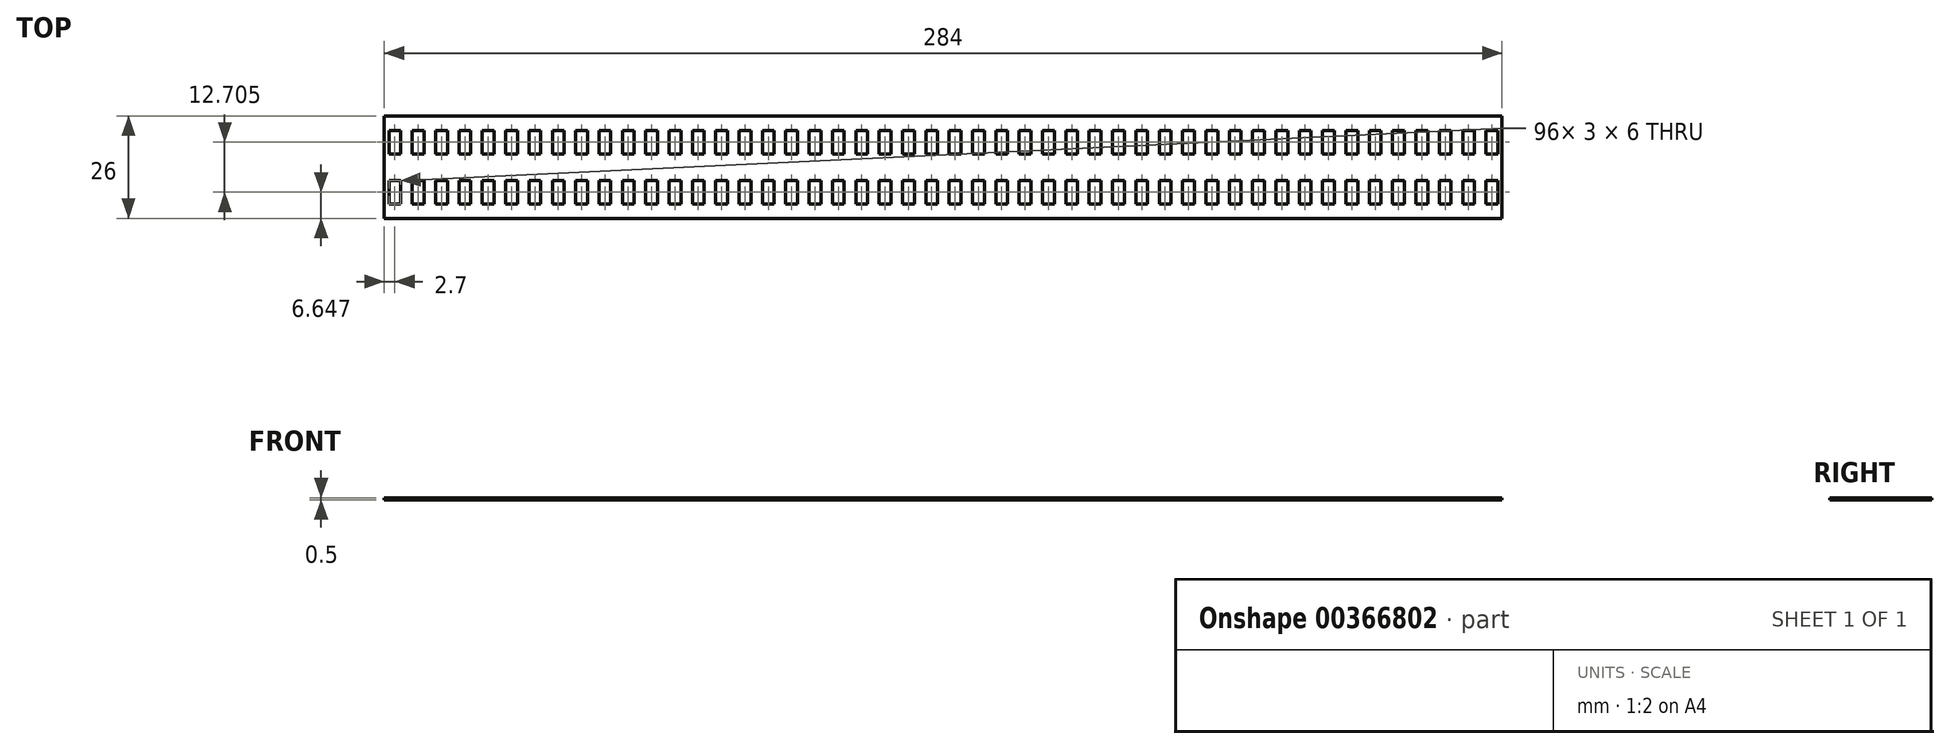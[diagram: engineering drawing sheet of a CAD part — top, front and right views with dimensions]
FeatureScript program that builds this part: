
annotation { "Feature Type Name" : "Feature", "Feature Type Description" : "" }
export const myFeature = defineFeature(function(context is Context, id is Id, definition is map)
    precondition{}
    {
        {
            var Q0;
            Q0=qCreatedBy(makeId("Top.planeOp"),FACE);
            var sketch = newSketch(context, id + "F0", { "sketchPlane" : qUnion([Q0])});
            skLineSegment(sketch, "E0.bottom", {"start": v(-142, -13) * mm, "end": v(142, -13) * mm});
            skLineSegment(sketch, "E0.top", {"start": v(-142, 13) * mm, "end": v(142, 13) * mm});
            skLineSegment(sketch, "E0.left", {"start": v(-142, -13) * mm, "end": v(-142, 13) * mm});
            skPoint(sketch, "E0.middle", {"position": v(0, 0) * mm});
            skLineSegment(sketch, "E1", {"start": v(142, 6.35) * mm, "end": v(-142, 6.35) * mm, "construction": true});
            skLineSegment(sketch, "E2.bottom", {"start": v(-140.8, 3.35) * mm, "end": v(-137.8, 3.35) * mm});
            skLineSegment(sketch, "E2.top", {"start": v(-140.8, 9.35) * mm, "end": v(-137.8, 9.35) * mm});
            skLineSegment(sketch, "E2.left", {"start": v(-140.8, 3.35) * mm, "end": v(-140.8, 9.35) * mm});
            skLineSegment(sketch, "E2.right", {"start": v(-137.8, 3.35) * mm, "end": v(-137.8, 9.35) * mm});
            skPoint(sketch, "E2.middle", {"position": v(-139.3, 6.35) * mm});
            skLineSegment(sketch, "E3.1.0.0", {"start": v(-134.87, 9.35) * mm, "end": v(-131.87, 9.35) * mm});
            skLineSegment(sketch, "E3.1.0.1", {"start": v(-134.87, 3.35) * mm, "end": v(-134.87, 9.35) * mm});
            skLineSegment(sketch, "E3.1.0.2", {"start": v(-134.87, 3.35) * mm, "end": v(-131.87, 3.35) * mm});
            skLineSegment(sketch, "E3.1.0.3", {"start": v(-131.87, 3.35) * mm, "end": v(-131.87, 9.35) * mm});
            skLineSegment(sketch, "E3.2.0.0", {"start": v(-128.94, 9.35) * mm, "end": v(-125.94, 9.35) * mm});
            skLineSegment(sketch, "E3.2.0.1", {"start": v(-128.94, 3.35) * mm, "end": v(-128.94, 9.35) * mm});
            skLineSegment(sketch, "E3.2.0.2", {"start": v(-128.94, 3.35) * mm, "end": v(-125.94, 3.35) * mm});
            skLineSegment(sketch, "E3.2.0.3", {"start": v(-125.94, 3.35) * mm, "end": v(-125.94, 9.35) * mm});
            skLineSegment(sketch, "E3.3.0.0", {"start": v(-123.01, 9.35) * mm, "end": v(-120.01, 9.35) * mm});
            skLineSegment(sketch, "E3.3.0.1", {"start": v(-123.01, 3.35) * mm, "end": v(-123.01, 9.35) * mm});
            skLineSegment(sketch, "E3.3.0.2", {"start": v(-123.01, 3.35) * mm, "end": v(-120.01, 3.35) * mm});
            skLineSegment(sketch, "E3.3.0.3", {"start": v(-120.01, 3.35) * mm, "end": v(-120.01, 9.35) * mm});
            skLineSegment(sketch, "E3.4.0.0", {"start": v(-117.08, 9.35) * mm, "end": v(-114.08, 9.35) * mm});
            skLineSegment(sketch, "E3.4.0.1", {"start": v(-117.08, 3.35) * mm, "end": v(-117.08, 9.35) * mm});
            skLineSegment(sketch, "E3.4.0.2", {"start": v(-117.08, 3.35) * mm, "end": v(-114.08, 3.35) * mm});
            skLineSegment(sketch, "E3.4.0.3", {"start": v(-114.08, 3.35) * mm, "end": v(-114.08, 9.35) * mm});
            skLineSegment(sketch, "E3.5.0.0", {"start": v(-111.15, 9.35) * mm, "end": v(-108.15, 9.35) * mm});
            skLineSegment(sketch, "E3.5.0.1", {"start": v(-111.15, 3.35) * mm, "end": v(-111.15, 9.35) * mm});
            skLineSegment(sketch, "E3.5.0.2", {"start": v(-111.15, 3.35) * mm, "end": v(-108.15, 3.35) * mm});
            skLineSegment(sketch, "E3.5.0.3", {"start": v(-108.15, 3.35) * mm, "end": v(-108.15, 9.35) * mm});
            skLineSegment(sketch, "E3.6.0.0", {"start": v(-105.22, 9.35) * mm, "end": v(-102.22, 9.35) * mm});
            skLineSegment(sketch, "E3.6.0.1", {"start": v(-105.22, 3.35) * mm, "end": v(-105.22, 9.35) * mm});
            skLineSegment(sketch, "E3.6.0.2", {"start": v(-105.22, 3.35) * mm, "end": v(-102.22, 3.35) * mm});
            skLineSegment(sketch, "E3.6.0.3", {"start": v(-102.22, 3.35) * mm, "end": v(-102.22, 9.35) * mm});
            skLineSegment(sketch, "E3.7.0.0", {"start": v(-99.3, 9.35) * mm, "end": v(-96.3, 9.35) * mm});
            skLineSegment(sketch, "E3.7.0.1", {"start": v(-99.3, 3.35) * mm, "end": v(-99.3, 9.35) * mm});
            skLineSegment(sketch, "E3.7.0.2", {"start": v(-99.3, 3.35) * mm, "end": v(-96.3, 3.35) * mm});
            skLineSegment(sketch, "E3.7.0.3", {"start": v(-96.3, 3.35) * mm, "end": v(-96.3, 9.35) * mm});
            skLineSegment(sketch, "E3.8.0.0", {"start": v(-93.36, 9.35) * mm, "end": v(-90.36, 9.35) * mm});
            skLineSegment(sketch, "E3.8.0.1", {"start": v(-93.36, 3.35) * mm, "end": v(-93.36, 9.35) * mm});
            skLineSegment(sketch, "E3.8.0.2", {"start": v(-93.36, 3.35) * mm, "end": v(-90.36, 3.35) * mm});
            skLineSegment(sketch, "E3.8.0.3", {"start": v(-90.36, 3.35) * mm, "end": v(-90.36, 9.35) * mm});
            skLineSegment(sketch, "E3.9.0.0", {"start": v(-87.43, 9.35) * mm, "end": v(-84.43, 9.35) * mm});
            skLineSegment(sketch, "E3.9.0.1", {"start": v(-87.43, 3.35) * mm, "end": v(-87.43, 9.35) * mm});
            skLineSegment(sketch, "E3.9.0.2", {"start": v(-87.43, 3.35) * mm, "end": v(-84.43, 3.35) * mm});
            skLineSegment(sketch, "E3.9.0.3", {"start": v(-84.43, 3.35) * mm, "end": v(-84.43, 9.35) * mm});
            skLineSegment(sketch, "E3.10.0.0", {"start": v(-81.5, 9.35) * mm, "end": v(-78.5, 9.35) * mm});
            skLineSegment(sketch, "E3.10.0.1", {"start": v(-81.5, 3.35) * mm, "end": v(-81.5, 9.35) * mm});
            skLineSegment(sketch, "E3.10.0.2", {"start": v(-81.5, 3.35) * mm, "end": v(-78.5, 3.35) * mm});
            skLineSegment(sketch, "E3.10.0.3", {"start": v(-78.5, 3.35) * mm, "end": v(-78.5, 9.35) * mm});
            skLineSegment(sketch, "E3.11.0.0", {"start": v(-75.57, 9.35) * mm, "end": v(-72.57, 9.35) * mm});
            skLineSegment(sketch, "E3.11.0.1", {"start": v(-75.57, 3.35) * mm, "end": v(-75.57, 9.35) * mm});
            skLineSegment(sketch, "E3.11.0.2", {"start": v(-75.57, 3.35) * mm, "end": v(-72.57, 3.35) * mm});
            skLineSegment(sketch, "E3.11.0.3", {"start": v(-72.57, 3.35) * mm, "end": v(-72.57, 9.35) * mm});
            skLineSegment(sketch, "E3.12.0.0", {"start": v(-69.64, 9.35) * mm, "end": v(-66.64, 9.35) * mm});
            skLineSegment(sketch, "E3.12.0.1", {"start": v(-69.64, 3.35) * mm, "end": v(-69.64, 9.35) * mm});
            skLineSegment(sketch, "E3.12.0.2", {"start": v(-69.64, 3.35) * mm, "end": v(-66.64, 3.35) * mm});
            skLineSegment(sketch, "E3.12.0.3", {"start": v(-66.64, 3.35) * mm, "end": v(-66.64, 9.35) * mm});
            skLineSegment(sketch, "E3.13.0.0", {"start": v(-63.71, 9.35) * mm, "end": v(-60.71, 9.35) * mm});
            skLineSegment(sketch, "E3.13.0.1", {"start": v(-63.71, 3.35) * mm, "end": v(-63.71, 9.35) * mm});
            skLineSegment(sketch, "E3.13.0.2", {"start": v(-63.71, 3.35) * mm, "end": v(-60.71, 3.35) * mm});
            skLineSegment(sketch, "E3.13.0.3", {"start": v(-60.71, 3.35) * mm, "end": v(-60.71, 9.35) * mm});
            skLineSegment(sketch, "E3.14.0.0", {"start": v(-57.78, 9.35) * mm, "end": v(-54.78, 9.35) * mm});
            skLineSegment(sketch, "E3.14.0.1", {"start": v(-57.78, 3.35) * mm, "end": v(-57.78, 9.35) * mm});
            skLineSegment(sketch, "E3.14.0.2", {"start": v(-57.78, 3.35) * mm, "end": v(-54.78, 3.35) * mm});
            skLineSegment(sketch, "E3.14.0.3", {"start": v(-54.78, 3.35) * mm, "end": v(-54.78, 9.35) * mm});
            skLineSegment(sketch, "E3.15.0.0", {"start": v(-51.85, 9.35) * mm, "end": v(-48.85, 9.35) * mm});
            skLineSegment(sketch, "E3.15.0.1", {"start": v(-51.85, 3.35) * mm, "end": v(-51.85, 9.35) * mm});
            skLineSegment(sketch, "E3.15.0.2", {"start": v(-51.85, 3.35) * mm, "end": v(-48.85, 3.35) * mm});
            skLineSegment(sketch, "E3.15.0.3", {"start": v(-48.85, 3.35) * mm, "end": v(-48.85, 9.35) * mm});
            skLineSegment(sketch, "E3.16.0.0", {"start": v(-45.92, 9.35) * mm, "end": v(-42.92, 9.35) * mm});
            skLineSegment(sketch, "E3.16.0.1", {"start": v(-45.92, 3.35) * mm, "end": v(-45.92, 9.35) * mm});
            skLineSegment(sketch, "E3.16.0.2", {"start": v(-45.92, 3.35) * mm, "end": v(-42.92, 3.35) * mm});
            skLineSegment(sketch, "E3.16.0.3", {"start": v(-42.92, 3.35) * mm, "end": v(-42.92, 9.35) * mm});
            skLineSegment(sketch, "E3.17.0.0", {"start": v(-40, 9.35) * mm, "end": v(-37, 9.35) * mm});
            skLineSegment(sketch, "E3.17.0.1", {"start": v(-40, 3.35) * mm, "end": v(-40, 9.35) * mm});
            skLineSegment(sketch, "E3.17.0.2", {"start": v(-40, 3.35) * mm, "end": v(-37, 3.35) * mm});
            skLineSegment(sketch, "E3.17.0.3", {"start": v(-37, 3.35) * mm, "end": v(-37, 9.35) * mm});
            skLineSegment(sketch, "E3.18.0.0", {"start": v(-34.06, 9.35) * mm, "end": v(-31.06, 9.35) * mm});
            skLineSegment(sketch, "E3.18.0.1", {"start": v(-34.06, 3.35) * mm, "end": v(-34.06, 9.35) * mm});
            skLineSegment(sketch, "E3.18.0.2", {"start": v(-34.06, 3.35) * mm, "end": v(-31.06, 3.35) * mm});
            skLineSegment(sketch, "E3.18.0.3", {"start": v(-31.06, 3.35) * mm, "end": v(-31.06, 9.35) * mm});
            skLineSegment(sketch, "E3.19.0.0", {"start": v(-28.13, 9.35) * mm, "end": v(-25.13, 9.35) * mm});
            skLineSegment(sketch, "E3.19.0.1", {"start": v(-28.13, 3.35) * mm, "end": v(-28.13, 9.35) * mm});
            skLineSegment(sketch, "E3.19.0.2", {"start": v(-28.13, 3.35) * mm, "end": v(-25.13, 3.35) * mm});
            skLineSegment(sketch, "E3.19.0.3", {"start": v(-25.13, 3.35) * mm, "end": v(-25.13, 9.35) * mm});
            skLineSegment(sketch, "E3.20.0.0", {"start": v(-22.2, 9.35) * mm, "end": v(-19.2, 9.35) * mm});
            skLineSegment(sketch, "E3.20.0.1", {"start": v(-22.2, 3.35) * mm, "end": v(-22.2, 9.35) * mm});
            skLineSegment(sketch, "E3.20.0.2", {"start": v(-22.2, 3.35) * mm, "end": v(-19.2, 3.35) * mm});
            skLineSegment(sketch, "E3.20.0.3", {"start": v(-19.2, 3.35) * mm, "end": v(-19.2, 9.35) * mm});
            skLineSegment(sketch, "E3.21.0.0", {"start": v(-16.27, 9.35) * mm, "end": v(-13.27, 9.35) * mm});
            skLineSegment(sketch, "E3.21.0.1", {"start": v(-16.27, 3.35) * mm, "end": v(-16.27, 9.35) * mm});
            skLineSegment(sketch, "E3.21.0.2", {"start": v(-16.27, 3.35) * mm, "end": v(-13.27, 3.35) * mm});
            skLineSegment(sketch, "E3.21.0.3", {"start": v(-13.27, 3.35) * mm, "end": v(-13.27, 9.35) * mm});
            skLineSegment(sketch, "E3.22.0.0", {"start": v(-10.34, 9.35) * mm, "end": v(-7.34, 9.35) * mm});
            skLineSegment(sketch, "E3.22.0.1", {"start": v(-10.34, 3.35) * mm, "end": v(-10.34, 9.35) * mm});
            skLineSegment(sketch, "E3.22.0.2", {"start": v(-10.34, 3.35) * mm, "end": v(-7.34, 3.35) * mm});
            skLineSegment(sketch, "E3.22.0.3", {"start": v(-7.34, 3.35) * mm, "end": v(-7.34, 9.35) * mm});
            skLineSegment(sketch, "E3.23.0.0", {"start": v(-4.41, 9.35) * mm, "end": v(-1.41, 9.35) * mm});
            skLineSegment(sketch, "E3.23.0.1", {"start": v(-4.41, 3.35) * mm, "end": v(-4.41, 9.35) * mm});
            skLineSegment(sketch, "E3.23.0.2", {"start": v(-4.41, 3.35) * mm, "end": v(-1.41, 3.35) * mm});
            skLineSegment(sketch, "E3.23.0.3", {"start": v(-1.41, 3.35) * mm, "end": v(-1.41, 9.35) * mm});
            skLineSegment(sketch, "E3.24.0.0", {"start": v(1.52, 9.35) * mm, "end": v(4.52, 9.35) * mm});
            skLineSegment(sketch, "E3.24.0.1", {"start": v(1.52, 3.35) * mm, "end": v(1.52, 9.35) * mm});
            skLineSegment(sketch, "E3.24.0.2", {"start": v(1.52, 3.35) * mm, "end": v(4.52, 3.35) * mm});
            skLineSegment(sketch, "E3.24.0.3", {"start": v(4.52, 3.35) * mm, "end": v(4.52, 9.35) * mm});
            skLineSegment(sketch, "E3.25.0.0", {"start": v(7.45, 9.35) * mm, "end": v(10.45, 9.35) * mm});
            skLineSegment(sketch, "E3.25.0.1", {"start": v(7.45, 3.35) * mm, "end": v(7.45, 9.35) * mm});
            skLineSegment(sketch, "E3.25.0.2", {"start": v(7.45, 3.35) * mm, "end": v(10.45, 3.35) * mm});
            skLineSegment(sketch, "E3.25.0.3", {"start": v(10.45, 3.35) * mm, "end": v(10.45, 9.35) * mm});
            skLineSegment(sketch, "E3.26.0.0", {"start": v(13.38, 9.35) * mm, "end": v(16.38, 9.35) * mm});
            skLineSegment(sketch, "E3.26.0.1", {"start": v(13.38, 3.35) * mm, "end": v(13.38, 9.35) * mm});
            skLineSegment(sketch, "E3.26.0.2", {"start": v(13.38, 3.35) * mm, "end": v(16.38, 3.35) * mm});
            skLineSegment(sketch, "E3.26.0.3", {"start": v(16.38, 3.35) * mm, "end": v(16.38, 9.35) * mm});
            skLineSegment(sketch, "E3.27.0.0", {"start": v(19.3, 9.35) * mm, "end": v(22.3, 9.35) * mm});
            skLineSegment(sketch, "E3.27.0.1", {"start": v(19.3, 3.35) * mm, "end": v(19.3, 9.35) * mm});
            skLineSegment(sketch, "E3.27.0.2", {"start": v(19.3, 3.35) * mm, "end": v(22.3, 3.35) * mm});
            skLineSegment(sketch, "E3.27.0.3", {"start": v(22.3, 3.35) * mm, "end": v(22.3, 9.35) * mm});
            skLineSegment(sketch, "E3.28.0.0", {"start": v(25.24, 9.35) * mm, "end": v(28.24, 9.35) * mm});
            skLineSegment(sketch, "E3.28.0.1", {"start": v(25.24, 3.35) * mm, "end": v(25.24, 9.35) * mm});
            skLineSegment(sketch, "E3.28.0.2", {"start": v(25.24, 3.35) * mm, "end": v(28.24, 3.35) * mm});
            skLineSegment(sketch, "E3.28.0.3", {"start": v(28.24, 3.35) * mm, "end": v(28.24, 9.35) * mm});
            skLineSegment(sketch, "E3.29.0.0", {"start": v(31.17, 9.35) * mm, "end": v(34.17, 9.35) * mm});
            skLineSegment(sketch, "E3.29.0.1", {"start": v(31.17, 3.35) * mm, "end": v(31.17, 9.35) * mm});
            skLineSegment(sketch, "E3.29.0.2", {"start": v(31.17, 3.35) * mm, "end": v(34.17, 3.35) * mm});
            skLineSegment(sketch, "E3.29.0.3", {"start": v(34.17, 3.35) * mm, "end": v(34.17, 9.35) * mm});
            skLineSegment(sketch, "E3.30.0.0", {"start": v(37.1, 9.35) * mm, "end": v(40.1, 9.35) * mm});
            skLineSegment(sketch, "E3.30.0.1", {"start": v(37.1, 3.35) * mm, "end": v(37.1, 9.35) * mm});
            skLineSegment(sketch, "E3.30.0.2", {"start": v(37.1, 3.35) * mm, "end": v(40.1, 3.35) * mm});
            skLineSegment(sketch, "E3.30.0.3", {"start": v(40.1, 3.35) * mm, "end": v(40.1, 9.35) * mm});
            skLineSegment(sketch, "E3.31.0.0", {"start": v(43.03, 9.35) * mm, "end": v(46.03, 9.35) * mm});
            skLineSegment(sketch, "E3.31.0.1", {"start": v(43.03, 3.35) * mm, "end": v(43.03, 9.35) * mm});
            skLineSegment(sketch, "E3.31.0.2", {"start": v(43.03, 3.35) * mm, "end": v(46.03, 3.35) * mm});
            skLineSegment(sketch, "E3.31.0.3", {"start": v(46.03, 3.35) * mm, "end": v(46.03, 9.35) * mm});
            skLineSegment(sketch, "E3.32.0.0", {"start": v(48.96, 9.35) * mm, "end": v(51.96, 9.35) * mm});
            skLineSegment(sketch, "E3.32.0.1", {"start": v(48.96, 3.35) * mm, "end": v(48.96, 9.35) * mm});
            skLineSegment(sketch, "E3.32.0.2", {"start": v(48.96, 3.35) * mm, "end": v(51.96, 3.35) * mm});
            skLineSegment(sketch, "E3.32.0.3", {"start": v(51.96, 3.35) * mm, "end": v(51.96, 9.35) * mm});
            skLineSegment(sketch, "E3.33.0.0", {"start": v(54.89, 9.35) * mm, "end": v(57.89, 9.35) * mm});
            skLineSegment(sketch, "E3.33.0.1", {"start": v(54.89, 3.35) * mm, "end": v(54.89, 9.35) * mm});
            skLineSegment(sketch, "E3.33.0.2", {"start": v(54.89, 3.35) * mm, "end": v(57.89, 3.35) * mm});
            skLineSegment(sketch, "E3.33.0.3", {"start": v(57.89, 3.35) * mm, "end": v(57.89, 9.35) * mm});
            skLineSegment(sketch, "E3.34.0.0", {"start": v(60.82, 9.35) * mm, "end": v(63.82, 9.35) * mm});
            skLineSegment(sketch, "E3.34.0.1", {"start": v(60.82, 3.35) * mm, "end": v(60.82, 9.35) * mm});
            skLineSegment(sketch, "E3.34.0.2", {"start": v(60.82, 3.35) * mm, "end": v(63.82, 3.35) * mm});
            skLineSegment(sketch, "E3.34.0.3", {"start": v(63.82, 3.35) * mm, "end": v(63.82, 9.35) * mm});
            skLineSegment(sketch, "E3.35.0.0", {"start": v(66.75, 9.35) * mm, "end": v(69.75, 9.35) * mm});
            skLineSegment(sketch, "E3.35.0.1", {"start": v(66.75, 3.35) * mm, "end": v(66.75, 9.35) * mm});
            skLineSegment(sketch, "E3.35.0.2", {"start": v(66.75, 3.35) * mm, "end": v(69.75, 3.35) * mm});
            skLineSegment(sketch, "E3.35.0.3", {"start": v(69.75, 3.35) * mm, "end": v(69.75, 9.35) * mm});
            skLineSegment(sketch, "E3.36.0.0", {"start": v(72.68, 9.35) * mm, "end": v(75.68, 9.35) * mm});
            skLineSegment(sketch, "E3.36.0.1", {"start": v(72.68, 3.35) * mm, "end": v(72.68, 9.35) * mm});
            skLineSegment(sketch, "E3.36.0.2", {"start": v(72.68, 3.35) * mm, "end": v(75.68, 3.35) * mm});
            skLineSegment(sketch, "E3.36.0.3", {"start": v(75.68, 3.35) * mm, "end": v(75.68, 9.35) * mm});
            skLineSegment(sketch, "E3.37.0.0", {"start": v(78.6, 9.35) * mm, "end": v(81.6, 9.35) * mm});
            skLineSegment(sketch, "E3.37.0.1", {"start": v(78.6, 3.35) * mm, "end": v(78.6, 9.35) * mm});
            skLineSegment(sketch, "E3.37.0.2", {"start": v(78.6, 3.35) * mm, "end": v(81.6, 3.35) * mm});
            skLineSegment(sketch, "E3.37.0.3", {"start": v(81.6, 3.35) * mm, "end": v(81.6, 9.35) * mm});
            skLineSegment(sketch, "E3.38.0.0", {"start": v(84.54, 9.35) * mm, "end": v(87.54, 9.35) * mm});
            skLineSegment(sketch, "E3.38.0.1", {"start": v(84.54, 3.35) * mm, "end": v(84.54, 9.35) * mm});
            skLineSegment(sketch, "E3.38.0.2", {"start": v(84.54, 3.35) * mm, "end": v(87.54, 3.35) * mm});
            skLineSegment(sketch, "E3.38.0.3", {"start": v(87.54, 3.35) * mm, "end": v(87.54, 9.35) * mm});
            skLineSegment(sketch, "E3.39.0.0", {"start": v(90.47, 9.35) * mm, "end": v(93.47, 9.35) * mm});
            skLineSegment(sketch, "E3.39.0.1", {"start": v(90.47, 3.35) * mm, "end": v(90.47, 9.35) * mm});
            skLineSegment(sketch, "E3.39.0.2", {"start": v(90.47, 3.35) * mm, "end": v(93.47, 3.35) * mm});
            skLineSegment(sketch, "E3.39.0.3", {"start": v(93.47, 3.35) * mm, "end": v(93.47, 9.35) * mm});
            skLineSegment(sketch, "E3.40.0.0", {"start": v(96.4, 9.35) * mm, "end": v(99.4, 9.35) * mm});
            skLineSegment(sketch, "E3.40.0.1", {"start": v(96.4, 3.35) * mm, "end": v(96.4, 9.35) * mm});
            skLineSegment(sketch, "E3.40.0.2", {"start": v(96.4, 3.35) * mm, "end": v(99.4, 3.35) * mm});
            skLineSegment(sketch, "E3.40.0.3", {"start": v(99.4, 3.35) * mm, "end": v(99.4, 9.35) * mm});
            skLineSegment(sketch, "E3.41.0.0", {"start": v(102.33, 9.35) * mm, "end": v(105.33, 9.35) * mm});
            skLineSegment(sketch, "E3.41.0.1", {"start": v(102.33, 3.35) * mm, "end": v(102.33, 9.35) * mm});
            skLineSegment(sketch, "E3.41.0.2", {"start": v(102.33, 3.35) * mm, "end": v(105.33, 3.35) * mm});
            skLineSegment(sketch, "E3.41.0.3", {"start": v(105.33, 3.35) * mm, "end": v(105.33, 9.35) * mm});
            skLineSegment(sketch, "E3.42.0.0", {"start": v(108.26, 9.35) * mm, "end": v(111.26, 9.35) * mm});
            skLineSegment(sketch, "E3.42.0.1", {"start": v(108.26, 3.35) * mm, "end": v(108.26, 9.35) * mm});
            skLineSegment(sketch, "E3.42.0.2", {"start": v(108.26, 3.35) * mm, "end": v(111.26, 3.35) * mm});
            skLineSegment(sketch, "E3.42.0.3", {"start": v(111.26, 3.35) * mm, "end": v(111.26, 9.35) * mm});
            skLineSegment(sketch, "E3.43.0.0", {"start": v(114.19, 9.35) * mm, "end": v(117.19, 9.35) * mm});
            skLineSegment(sketch, "E3.43.0.1", {"start": v(114.19, 3.35) * mm, "end": v(114.19, 9.35) * mm});
            skLineSegment(sketch, "E3.43.0.2", {"start": v(114.19, 3.35) * mm, "end": v(117.19, 3.35) * mm});
            skLineSegment(sketch, "E3.43.0.3", {"start": v(117.19, 3.35) * mm, "end": v(117.19, 9.35) * mm});
            skLineSegment(sketch, "E3.44.0.0", {"start": v(120.12, 9.35) * mm, "end": v(123.12, 9.35) * mm});
            skLineSegment(sketch, "E3.44.0.1", {"start": v(120.12, 3.35) * mm, "end": v(120.12, 9.35) * mm});
            skLineSegment(sketch, "E3.44.0.2", {"start": v(120.12, 3.35) * mm, "end": v(123.12, 3.35) * mm});
            skLineSegment(sketch, "E3.44.0.3", {"start": v(123.12, 3.35) * mm, "end": v(123.12, 9.35) * mm});
            skLineSegment(sketch, "E3.45.0.0", {"start": v(126.05, 9.35) * mm, "end": v(129.05, 9.35) * mm});
            skLineSegment(sketch, "E3.45.0.1", {"start": v(126.05, 3.35) * mm, "end": v(126.05, 9.35) * mm});
            skLineSegment(sketch, "E3.45.0.2", {"start": v(126.05, 3.35) * mm, "end": v(129.05, 3.35) * mm});
            skLineSegment(sketch, "E3.45.0.3", {"start": v(129.05, 3.35) * mm, "end": v(129.05, 9.35) * mm});
            skLineSegment(sketch, "E3.46.0.0", {"start": v(131.98, 9.35) * mm, "end": v(134.98, 9.35) * mm});
            skLineSegment(sketch, "E3.46.0.1", {"start": v(131.98, 3.35) * mm, "end": v(131.98, 9.35) * mm});
            skLineSegment(sketch, "E3.46.0.2", {"start": v(131.98, 3.35) * mm, "end": v(134.98, 3.35) * mm});
            skLineSegment(sketch, "E3.46.0.3", {"start": v(134.98, 3.35) * mm, "end": v(134.98, 9.35) * mm});
            skLineSegment(sketch, "E3.47.0.0", {"start": v(137.9, 9.35) * mm, "end": v(140.9, 9.35) * mm});
            skLineSegment(sketch, "E3.47.0.1", {"start": v(137.9, 3.35) * mm, "end": v(137.9, 9.35) * mm});
            skLineSegment(sketch, "E3.47.0.2", {"start": v(137.9, 3.35) * mm, "end": v(140.9, 3.35) * mm});
            skLineSegment(sketch, "E3.47.0.3", {"start": v(140.9, 3.35) * mm, "end": v(140.9, 9.35) * mm});
            skLineSegment(sketch, "E3.direction1", {"start": v(-140.8, 9.35) * mm, "end": v(-134.87, 9.35) * mm, "construction": true});
            skLineSegment(sketch, "E4", {"start": v(-142, 0) * mm, "end": v(142, 0) * mm});
            skLineSegment(sketch, "E5", {"start": v(142, 13) * mm, "end": v(142, 0) * mm});
            skLineSegment(sketch, "E6", {"start": v(142, 0) * mm, "end": v(142, -13) * mm});
            skLineSegment(sketch, "E7.MirrorCS", {"start": v(90.47, -3.35) * mm, "end": v(90.47, -9.35) * mm});
            skLineSegment(sketch, "E8.MirrorCS", {"start": v(114.19, -3.35) * mm, "end": v(114.19, -9.35) * mm});
            skLineSegment(sketch, "E9.MirrorCS", {"start": v(137.9, -3.35) * mm, "end": v(137.9, -9.35) * mm});
            skLineSegment(sketch, "E10.MirrorCS", {"start": v(43.03, -3.35) * mm, "end": v(43.03, -9.35) * mm});
            skLineSegment(sketch, "E11.MirrorCS", {"start": v(66.75, -3.35) * mm, "end": v(66.75, -9.35) * mm});
            skLineSegment(sketch, "E12.MirrorCS", {"start": v(43.03, -9.35) * mm, "end": v(46.03, -9.35) * mm});
            skLineSegment(sketch, "E13.MirrorCS", {"start": v(66.75, -9.35) * mm, "end": v(69.75, -9.35) * mm});
            skLineSegment(sketch, "E14.MirrorCS", {"start": v(90.47, -9.35) * mm, "end": v(93.47, -9.35) * mm});
            skLineSegment(sketch, "E15.MirrorCS", {"start": v(114.19, -9.35) * mm, "end": v(117.19, -9.35) * mm});
            skLineSegment(sketch, "E16.MirrorCS", {"start": v(87.54, -3.35) * mm, "end": v(87.54, -9.35) * mm});
            skLineSegment(sketch, "E17.MirrorCS", {"start": v(111.26, -3.35) * mm, "end": v(111.26, -9.35) * mm});
            skLineSegment(sketch, "E18.MirrorCS", {"start": v(134.98, -3.35) * mm, "end": v(134.98, -9.35) * mm});
            skLineSegment(sketch, "E19.MirrorCS", {"start": v(40.1, -3.35) * mm, "end": v(40.1, -9.35) * mm});
            skLineSegment(sketch, "E20.MirrorCS", {"start": v(63.82, -3.35) * mm, "end": v(63.82, -9.35) * mm});
            skLineSegment(sketch, "E21.MirrorCS", {"start": v(84.54, -3.35) * mm, "end": v(87.54, -3.35) * mm});
            skLineSegment(sketch, "E22.MirrorCS", {"start": v(108.26, -3.35) * mm, "end": v(111.26, -3.35) * mm});
            skLineSegment(sketch, "E23.MirrorCS", {"start": v(131.98, -3.35) * mm, "end": v(134.98, -3.35) * mm});
            skLineSegment(sketch, "E24.MirrorCS", {"start": v(60.82, -3.35) * mm, "end": v(63.82, -3.35) * mm});
            skLineSegment(sketch, "E25.MirrorCS", {"start": v(84.54, -3.35) * mm, "end": v(84.54, -9.35) * mm});
            skLineSegment(sketch, "E26.MirrorCS", {"start": v(108.26, -3.35) * mm, "end": v(108.26, -9.35) * mm});
            skLineSegment(sketch, "E27.MirrorCS", {"start": v(131.98, -3.35) * mm, "end": v(131.98, -9.35) * mm});
            skLineSegment(sketch, "E28.MirrorCS", {"start": v(60.82, -3.35) * mm, "end": v(60.82, -9.35) * mm});
            skLineSegment(sketch, "E29.MirrorCS", {"start": v(57.89, -3.35) * mm, "end": v(57.89, -9.35) * mm});
            skLineSegment(sketch, "E30.MirrorCS", {"start": v(81.6, -3.35) * mm, "end": v(81.6, -9.35) * mm});
            skLineSegment(sketch, "E31.MirrorCS", {"start": v(105.33, -3.35) * mm, "end": v(105.33, -9.35) * mm});
            skLineSegment(sketch, "E32.MirrorCS", {"start": v(129.05, -3.35) * mm, "end": v(129.05, -9.35) * mm});
            skLineSegment(sketch, "E33.MirrorCS", {"start": v(84.54, -9.35) * mm, "end": v(87.54, -9.35) * mm});
            skLineSegment(sketch, "E34.MirrorCS", {"start": v(108.26, -9.35) * mm, "end": v(111.26, -9.35) * mm});
            skLineSegment(sketch, "E35.MirrorCS", {"start": v(131.98, -9.35) * mm, "end": v(134.98, -9.35) * mm});
            skLineSegment(sketch, "E36.MirrorCS", {"start": v(60.82, -9.35) * mm, "end": v(63.82, -9.35) * mm});
            skLineSegment(sketch, "E37.MirrorCS", {"start": v(54.89, -3.35) * mm, "end": v(57.89, -3.35) * mm});
            skLineSegment(sketch, "E38.MirrorCS", {"start": v(78.6, -3.35) * mm, "end": v(81.6, -3.35) * mm});
            skLineSegment(sketch, "E39.MirrorCS", {"start": v(102.33, -3.35) * mm, "end": v(105.33, -3.35) * mm});
            skLineSegment(sketch, "E40.MirrorCS", {"start": v(126.05, -3.35) * mm, "end": v(129.05, -3.35) * mm});
            skLineSegment(sketch, "E41.MirrorCS", {"start": v(54.89, -3.35) * mm, "end": v(54.89, -9.35) * mm});
            skLineSegment(sketch, "E42.MirrorCS", {"start": v(78.6, -3.35) * mm, "end": v(78.6, -9.35) * mm});
            skLineSegment(sketch, "E43.MirrorCS", {"start": v(126.05, -3.35) * mm, "end": v(126.05, -9.35) * mm});
            skLineSegment(sketch, "E44.MirrorCS", {"start": v(102.33, -3.35) * mm, "end": v(102.33, -9.35) * mm});
            skLineSegment(sketch, "E45.MirrorCS", {"start": v(54.89, -9.35) * mm, "end": v(57.89, -9.35) * mm});
            skLineSegment(sketch, "E46.MirrorCS", {"start": v(78.6, -9.35) * mm, "end": v(81.6, -9.35) * mm});
            skLineSegment(sketch, "E47.MirrorCS", {"start": v(102.33, -9.35) * mm, "end": v(105.33, -9.35) * mm});
            skLineSegment(sketch, "E48.MirrorCS", {"start": v(126.05, -9.35) * mm, "end": v(129.05, -9.35) * mm});
            skLineSegment(sketch, "E49.MirrorCS", {"start": v(51.96, -3.35) * mm, "end": v(51.96, -9.35) * mm});
            skLineSegment(sketch, "E50.MirrorCS", {"start": v(75.68, -3.35) * mm, "end": v(75.68, -9.35) * mm});
            skLineSegment(sketch, "E51.MirrorCS", {"start": v(99.4, -3.35) * mm, "end": v(99.4, -9.35) * mm});
            skLineSegment(sketch, "E52.MirrorCS", {"start": v(123.12, -3.35) * mm, "end": v(123.12, -9.35) * mm});
            skLineSegment(sketch, "E53.MirrorCS", {"start": v(48.96, -3.35) * mm, "end": v(51.96, -3.35) * mm});
            skLineSegment(sketch, "E54.MirrorCS", {"start": v(72.68, -3.35) * mm, "end": v(75.68, -3.35) * mm});
            skLineSegment(sketch, "E55.MirrorCS", {"start": v(96.4, -3.35) * mm, "end": v(99.4, -3.35) * mm});
            skLineSegment(sketch, "E56.MirrorCS", {"start": v(120.12, -3.35) * mm, "end": v(123.12, -3.35) * mm});
            skLineSegment(sketch, "E57.MirrorCS", {"start": v(96.4, -3.35) * mm, "end": v(96.4, -9.35) * mm});
            skLineSegment(sketch, "E58.MirrorCS", {"start": v(120.12, -3.35) * mm, "end": v(120.12, -9.35) * mm});
            skLineSegment(sketch, "E59.MirrorCS", {"start": v(48.96, -3.35) * mm, "end": v(48.96, -9.35) * mm});
            skLineSegment(sketch, "E60.MirrorCS", {"start": v(72.68, -3.35) * mm, "end": v(72.68, -9.35) * mm});
            skLineSegment(sketch, "E61.MirrorCS", {"start": v(96.4, -9.35) * mm, "end": v(99.4, -9.35) * mm});
            skLineSegment(sketch, "E62.MirrorCS", {"start": v(120.12, -9.35) * mm, "end": v(123.12, -9.35) * mm});
            skLineSegment(sketch, "E63.MirrorCS", {"start": v(48.96, -9.35) * mm, "end": v(51.96, -9.35) * mm});
            skLineSegment(sketch, "E64.MirrorCS", {"start": v(72.68, -9.35) * mm, "end": v(75.68, -9.35) * mm});
            skLineSegment(sketch, "E65.MirrorCS", {"start": v(93.47, -3.35) * mm, "end": v(93.47, -9.35) * mm});
            skLineSegment(sketch, "E66.MirrorCS", {"start": v(117.19, -3.35) * mm, "end": v(117.19, -9.35) * mm});
            skLineSegment(sketch, "E67.MirrorCS", {"start": v(46.03, -3.35) * mm, "end": v(46.03, -9.35) * mm});
            skLineSegment(sketch, "E68.MirrorCS", {"start": v(69.75, -3.35) * mm, "end": v(69.75, -9.35) * mm});
            skLineSegment(sketch, "E69.MirrorCS", {"start": v(90.47, -3.35) * mm, "end": v(93.47, -3.35) * mm});
            skLineSegment(sketch, "E70.MirrorCS", {"start": v(66.75, -3.35) * mm, "end": v(69.75, -3.35) * mm});
            skLineSegment(sketch, "E71.MirrorCS", {"start": v(114.19, -3.35) * mm, "end": v(117.19, -3.35) * mm});
            skLineSegment(sketch, "E72.MirrorCS", {"start": v(43.03, -3.35) * mm, "end": v(46.03, -3.35) * mm});
            skLineSegment(sketch, "E73.MirrorCS", {"start": v(137.9, -9.35) * mm, "end": v(140.9, -9.35) * mm});
            skLineSegment(sketch, "E74.MirrorCS", {"start": v(140.9, -3.35) * mm, "end": v(140.9, -9.35) * mm});
            skLineSegment(sketch, "E75.MirrorCS", {"start": v(137.9, -3.35) * mm, "end": v(140.9, -3.35) * mm});
            skLineSegment(sketch, "E76.MirrorCS", {"start": v(-128.94, -3.35) * mm, "end": v(-125.94, -3.35) * mm});
            skLineSegment(sketch, "E77.MirrorCS", {"start": v(-34.06, -9.35) * mm, "end": v(-31.06, -9.35) * mm});
            skLineSegment(sketch, "E78.MirrorCS", {"start": v(-57.78, -9.35) * mm, "end": v(-54.78, -9.35) * mm});
            skLineSegment(sketch, "E79.MirrorCS", {"start": v(-81.5, -9.35) * mm, "end": v(-78.5, -9.35) * mm});
            skLineSegment(sketch, "E80.MirrorCS", {"start": v(-105.22, -9.35) * mm, "end": v(-102.22, -9.35) * mm});
            skLineSegment(sketch, "E81.MirrorCS", {"start": v(37.1, -9.35) * mm, "end": v(40.1, -9.35) * mm});
            skLineSegment(sketch, "E82.MirrorCS", {"start": v(13.38, -9.35) * mm, "end": v(16.38, -9.35) * mm});
            skLineSegment(sketch, "E83.MirrorCS", {"start": v(-10.34, -9.35) * mm, "end": v(-7.34, -9.35) * mm});
            skLineSegment(sketch, "E84.MirrorCS", {"start": v(-34.06, -3.35) * mm, "end": v(-31.06, -3.35) * mm});
            skLineSegment(sketch, "E85.MirrorCS", {"start": v(-57.78, -3.35) * mm, "end": v(-54.78, -3.35) * mm});
            skLineSegment(sketch, "E86.MirrorCS", {"start": v(-81.5, -3.35) * mm, "end": v(-78.5, -3.35) * mm});
            skLineSegment(sketch, "E87.MirrorCS", {"start": v(-105.22, -3.35) * mm, "end": v(-102.22, -3.35) * mm});
            skLineSegment(sketch, "E88.MirrorCS", {"start": v(37.1, -3.35) * mm, "end": v(40.1, -3.35) * mm});
            skLineSegment(sketch, "E89.MirrorCS", {"start": v(13.38, -3.35) * mm, "end": v(16.38, -3.35) * mm});
            skLineSegment(sketch, "E90.MirrorCS", {"start": v(-10.34, -3.35) * mm, "end": v(-7.34, -3.35) * mm});
            skLineSegment(sketch, "E91.MirrorCS", {"start": v(-69.64, -9.35) * mm, "end": v(-66.64, -9.35) * mm});
            skLineSegment(sketch, "E92.MirrorCS", {"start": v(-93.36, -9.35) * mm, "end": v(-90.36, -9.35) * mm});
            skLineSegment(sketch, "E93.MirrorCS", {"start": v(-45.92, -9.35) * mm, "end": v(-42.92, -9.35) * mm});
            skLineSegment(sketch, "E94.MirrorCS", {"start": v(-22.2, -9.35) * mm, "end": v(-19.2, -9.35) * mm});
            skLineSegment(sketch, "E95.MirrorCS", {"start": v(-117.08, -9.35) * mm, "end": v(-114.08, -9.35) * mm});
            skLineSegment(sketch, "E96.MirrorCS", {"start": v(-4.41, -3.35) * mm, "end": v(-1.41, -3.35) * mm});
            skLineSegment(sketch, "E97.MirrorCS", {"start": v(19.3, -3.35) * mm, "end": v(22.3, -3.35) * mm});
            skLineSegment(sketch, "E98.MirrorCS", {"start": v(-99.3, -3.35) * mm, "end": v(-96.3, -3.35) * mm});
            skLineSegment(sketch, "E99.MirrorCS", {"start": v(-75.57, -3.35) * mm, "end": v(-72.57, -3.35) * mm});
            skLineSegment(sketch, "E100.MirrorCS", {"start": v(-51.85, -3.35) * mm, "end": v(-48.85, -3.35) * mm});
            skLineSegment(sketch, "E101.MirrorCS", {"start": v(-28.13, -3.35) * mm, "end": v(-25.13, -3.35) * mm});
            skLineSegment(sketch, "E102.MirrorCS", {"start": v(-123.01, -3.35) * mm, "end": v(-120.01, -3.35) * mm});
            skLineSegment(sketch, "E103.MirrorCS", {"start": v(-128.94, -9.35) * mm, "end": v(-125.94, -9.35) * mm});
            skLineSegment(sketch, "E104.MirrorCS", {"start": v(1.52, -9.35) * mm, "end": v(4.52, -9.35) * mm});
            skLineSegment(sketch, "E105.MirrorCS", {"start": v(-4.41, -9.35) * mm, "end": v(-1.41, -9.35) * mm});
            skLineSegment(sketch, "E106.MirrorCS", {"start": v(19.3, -9.35) * mm, "end": v(22.3, -9.35) * mm});
            skLineSegment(sketch, "E107.MirrorCS", {"start": v(-99.3, -9.35) * mm, "end": v(-96.3, -9.35) * mm});
            skLineSegment(sketch, "E108.MirrorCS", {"start": v(-75.57, -9.35) * mm, "end": v(-72.57, -9.35) * mm});
            skLineSegment(sketch, "E109.MirrorCS", {"start": v(-51.85, -9.35) * mm, "end": v(-48.85, -9.35) * mm});
            skLineSegment(sketch, "E110.MirrorCS", {"start": v(-28.13, -9.35) * mm, "end": v(-25.13, -9.35) * mm});
            skLineSegment(sketch, "E111.MirrorCS", {"start": v(-123.01, -9.35) * mm, "end": v(-120.01, -9.35) * mm});
            skLineSegment(sketch, "E112.MirrorCS", {"start": v(-40, -3.35) * mm, "end": v(-37, -3.35) * mm});
            skLineSegment(sketch, "E113.MirrorCS", {"start": v(-16.27, -3.35) * mm, "end": v(-13.27, -3.35) * mm});
            skLineSegment(sketch, "E114.MirrorCS", {"start": v(7.45, -3.35) * mm, "end": v(10.45, -3.35) * mm});
            skLineSegment(sketch, "E115.MirrorCS", {"start": v(31.17, -3.35) * mm, "end": v(34.17, -3.35) * mm});
            skLineSegment(sketch, "E116.MirrorCS", {"start": v(-111.15, -3.35) * mm, "end": v(-108.15, -3.35) * mm});
            skLineSegment(sketch, "E117.MirrorCS", {"start": v(-87.43, -3.35) * mm, "end": v(-84.43, -3.35) * mm});
            skLineSegment(sketch, "E118.MirrorCS", {"start": v(-63.71, -3.35) * mm, "end": v(-60.71, -3.35) * mm});
            skLineSegment(sketch, "E119.MirrorCS", {"start": v(-40, -9.35) * mm, "end": v(-37, -9.35) * mm});
            skLineSegment(sketch, "E120.MirrorCS", {"start": v(-16.27, -9.35) * mm, "end": v(-13.27, -9.35) * mm});
            skLineSegment(sketch, "E121.MirrorCS", {"start": v(7.45, -9.35) * mm, "end": v(10.45, -9.35) * mm});
            skLineSegment(sketch, "E122.MirrorCS", {"start": v(31.17, -9.35) * mm, "end": v(34.17, -9.35) * mm});
            skLineSegment(sketch, "E123.MirrorCS", {"start": v(-111.15, -9.35) * mm, "end": v(-108.15, -9.35) * mm});
            skLineSegment(sketch, "E124.MirrorCS", {"start": v(-87.43, -9.35) * mm, "end": v(-84.43, -9.35) * mm});
            skLineSegment(sketch, "E125.MirrorCS", {"start": v(-63.71, -9.35) * mm, "end": v(-60.71, -9.35) * mm});
            skLineSegment(sketch, "E126.MirrorCS", {"start": v(-45.92, -3.35) * mm, "end": v(-42.92, -3.35) * mm});
            skLineSegment(sketch, "E127.MirrorCS", {"start": v(-22.2, -3.35) * mm, "end": v(-19.2, -3.35) * mm});
            skLineSegment(sketch, "E128.MirrorCS", {"start": v(1.52, -3.35) * mm, "end": v(4.52, -3.35) * mm});
            skLineSegment(sketch, "E129.MirrorCS", {"start": v(25.24, -3.35) * mm, "end": v(28.24, -3.35) * mm});
            skLineSegment(sketch, "E130.MirrorCS", {"start": v(-117.08, -3.35) * mm, "end": v(-114.08, -3.35) * mm});
            skLineSegment(sketch, "E131.MirrorCS", {"start": v(-93.36, -3.35) * mm, "end": v(-90.36, -3.35) * mm});
            skLineSegment(sketch, "E132.MirrorCS", {"start": v(-69.64, -3.35) * mm, "end": v(-66.64, -3.35) * mm});
            skLineSegment(sketch, "E133.MirrorCS", {"start": v(25.24, -9.35) * mm, "end": v(28.24, -9.35) * mm});
            skLineSegment(sketch, "E134.MirrorCS", {"start": v(-34.06, -3.35) * mm, "end": v(-34.06, -9.35) * mm});
            skLineSegment(sketch, "E135.MirrorCS", {"start": v(-57.78, -3.35) * mm, "end": v(-57.78, -9.35) * mm});
            skLineSegment(sketch, "E136.MirrorCS", {"start": v(-81.5, -3.35) * mm, "end": v(-81.5, -9.35) * mm});
            skLineSegment(sketch, "E137.MirrorCS", {"start": v(-105.22, -3.35) * mm, "end": v(-105.22, -9.35) * mm});
            skLineSegment(sketch, "E138.MirrorCS", {"start": v(37.1, -3.35) * mm, "end": v(37.1, -9.35) * mm});
            skLineSegment(sketch, "E139.MirrorCS", {"start": v(13.38, -3.35) * mm, "end": v(13.38, -9.35) * mm});
            skLineSegment(sketch, "E140.MirrorCS", {"start": v(-10.34, -3.35) * mm, "end": v(-10.34, -9.35) * mm});
            skLineSegment(sketch, "E141.MirrorCS", {"start": v(16.38, -3.35) * mm, "end": v(16.38, -9.35) * mm});
            skLineSegment(sketch, "E142.MirrorCS", {"start": v(-7.34, -3.35) * mm, "end": v(-7.34, -9.35) * mm});
            skLineSegment(sketch, "E143.MirrorCS", {"start": v(-125.94, -3.35) * mm, "end": v(-125.94, -9.35) * mm});
            skLineSegment(sketch, "E144.MirrorCS", {"start": v(-31.06, -3.35) * mm, "end": v(-31.06, -9.35) * mm});
            skLineSegment(sketch, "E145.MirrorCS", {"start": v(-54.78, -3.35) * mm, "end": v(-54.78, -9.35) * mm});
            skLineSegment(sketch, "E146.MirrorCS", {"start": v(-78.5, -3.35) * mm, "end": v(-78.5, -9.35) * mm});
            skLineSegment(sketch, "E147.MirrorCS", {"start": v(-102.22, -3.35) * mm, "end": v(-102.22, -9.35) * mm});
            skLineSegment(sketch, "E148.MirrorCS", {"start": v(-1.41, -3.35) * mm, "end": v(-1.41, -9.35) * mm});
            skLineSegment(sketch, "E149.MirrorCS", {"start": v(22.3, -3.35) * mm, "end": v(22.3, -9.35) * mm});
            skLineSegment(sketch, "E150.MirrorCS", {"start": v(-96.3, -3.35) * mm, "end": v(-96.3, -9.35) * mm});
            skLineSegment(sketch, "E151.MirrorCS", {"start": v(-72.57, -3.35) * mm, "end": v(-72.57, -9.35) * mm});
            skLineSegment(sketch, "E152.MirrorCS", {"start": v(-48.85, -3.35) * mm, "end": v(-48.85, -9.35) * mm});
            skLineSegment(sketch, "E153.MirrorCS", {"start": v(-25.13, -3.35) * mm, "end": v(-25.13, -9.35) * mm});
            skLineSegment(sketch, "E154.MirrorCS", {"start": v(-120.01, -3.35) * mm, "end": v(-120.01, -9.35) * mm});
            skLineSegment(sketch, "E155.MirrorCS", {"start": v(-128.94, -3.35) * mm, "end": v(-128.94, -9.35) * mm});
            skLineSegment(sketch, "E156.MirrorCS", {"start": v(-4.41, -3.35) * mm, "end": v(-4.41, -9.35) * mm});
            skLineSegment(sketch, "E157.MirrorCS", {"start": v(19.3, -3.35) * mm, "end": v(19.3, -9.35) * mm});
            skLineSegment(sketch, "E158.MirrorCS", {"start": v(-75.57, -3.35) * mm, "end": v(-75.57, -9.35) * mm});
            skLineSegment(sketch, "E159.MirrorCS", {"start": v(-99.3, -3.35) * mm, "end": v(-99.3, -9.35) * mm});
            skLineSegment(sketch, "E160.MirrorCS", {"start": v(-51.85, -3.35) * mm, "end": v(-51.85, -9.35) * mm});
            skLineSegment(sketch, "E161.MirrorCS", {"start": v(-28.13, -3.35) * mm, "end": v(-28.13, -9.35) * mm});
            skLineSegment(sketch, "E162.MirrorCS", {"start": v(-37, -3.35) * mm, "end": v(-37, -9.35) * mm});
            skLineSegment(sketch, "E163.MirrorCS", {"start": v(-123.01, -3.35) * mm, "end": v(-123.01, -9.35) * mm});
            skLineSegment(sketch, "E164.MirrorCS", {"start": v(-13.27, -3.35) * mm, "end": v(-13.27, -9.35) * mm});
            skLineSegment(sketch, "E165.MirrorCS", {"start": v(10.45, -3.35) * mm, "end": v(10.45, -9.35) * mm});
            skLineSegment(sketch, "E166.MirrorCS", {"start": v(34.17, -3.35) * mm, "end": v(34.17, -9.35) * mm});
            skLineSegment(sketch, "E167.MirrorCS", {"start": v(-108.15, -3.35) * mm, "end": v(-108.15, -9.35) * mm});
            skLineSegment(sketch, "E168.MirrorCS", {"start": v(-84.43, -3.35) * mm, "end": v(-84.43, -9.35) * mm});
            skLineSegment(sketch, "E169.MirrorCS", {"start": v(-60.71, -3.35) * mm, "end": v(-60.71, -9.35) * mm});
            skLineSegment(sketch, "E170.MirrorCS", {"start": v(-40, -3.35) * mm, "end": v(-40, -9.35) * mm});
            skLineSegment(sketch, "E171.MirrorCS", {"start": v(-16.27, -3.35) * mm, "end": v(-16.27, -9.35) * mm});
            skLineSegment(sketch, "E172.MirrorCS", {"start": v(7.45, -3.35) * mm, "end": v(7.45, -9.35) * mm});
            skLineSegment(sketch, "E173.MirrorCS", {"start": v(31.17, -3.35) * mm, "end": v(31.17, -9.35) * mm});
            skLineSegment(sketch, "E174.MirrorCS", {"start": v(-111.15, -3.35) * mm, "end": v(-111.15, -9.35) * mm});
            skLineSegment(sketch, "E175.MirrorCS", {"start": v(-87.43, -3.35) * mm, "end": v(-87.43, -9.35) * mm});
            skLineSegment(sketch, "E176.MirrorCS", {"start": v(-63.71, -3.35) * mm, "end": v(-63.71, -9.35) * mm});
            skLineSegment(sketch, "E177.MirrorCS", {"start": v(-42.92, -3.35) * mm, "end": v(-42.92, -9.35) * mm});
            skLineSegment(sketch, "E178.MirrorCS", {"start": v(-19.2, -3.35) * mm, "end": v(-19.2, -9.35) * mm});
            skLineSegment(sketch, "E179.MirrorCS", {"start": v(4.52, -3.35) * mm, "end": v(4.52, -9.35) * mm});
            skLineSegment(sketch, "E180.MirrorCS", {"start": v(28.24, -3.35) * mm, "end": v(28.24, -9.35) * mm});
            skLineSegment(sketch, "E181.MirrorCS", {"start": v(-114.08, -3.35) * mm, "end": v(-114.08, -9.35) * mm});
            skLineSegment(sketch, "E182.MirrorCS", {"start": v(-90.36, -3.35) * mm, "end": v(-90.36, -9.35) * mm});
            skLineSegment(sketch, "E183.MirrorCS", {"start": v(-66.64, -3.35) * mm, "end": v(-66.64, -9.35) * mm});
            skLineSegment(sketch, "E184.MirrorCS", {"start": v(1.52, -3.35) * mm, "end": v(1.52, -9.35) * mm});
            skLineSegment(sketch, "E185.MirrorCS", {"start": v(25.24, -3.35) * mm, "end": v(25.24, -9.35) * mm});
            skLineSegment(sketch, "E186.MirrorCS", {"start": v(-93.36, -3.35) * mm, "end": v(-93.36, -9.35) * mm});
            skLineSegment(sketch, "E187.MirrorCS", {"start": v(-69.64, -3.35) * mm, "end": v(-69.64, -9.35) * mm});
            skLineSegment(sketch, "E188.MirrorCS", {"start": v(-117.08, -3.35) * mm, "end": v(-117.08, -9.35) * mm});
            skLineSegment(sketch, "E189.MirrorCS", {"start": v(-22.2, -3.35) * mm, "end": v(-22.2, -9.35) * mm});
            skLineSegment(sketch, "E190.MirrorCS", {"start": v(-45.92, -3.35) * mm, "end": v(-45.92, -9.35) * mm});
            skLineSegment(sketch, "E191.MirrorCS", {"start": v(142, -6.35) * mm, "end": v(-142, -6.35) * mm, "construction": true});
            skLineSegment(sketch, "E192.MirrorCS", {"start": v(-140.8, -9.35) * mm, "end": v(-137.8, -9.35) * mm});
            skLineSegment(sketch, "E193.MirrorCS", {"start": v(-131.87, -3.35) * mm, "end": v(-131.87, -9.35) * mm});
            skLineSegment(sketch, "E194.MirrorCS", {"start": v(-134.87, -3.35) * mm, "end": v(-131.87, -3.35) * mm});
            skLineSegment(sketch, "E195.MirrorCS", {"start": v(-134.87, -3.35) * mm, "end": v(-134.87, -9.35) * mm});
            skLineSegment(sketch, "E196.MirrorCS", {"start": v(-134.87, -9.35) * mm, "end": v(-131.87, -9.35) * mm});
            skLineSegment(sketch, "E197.MirrorCS", {"start": v(-137.8, -3.35) * mm, "end": v(-137.8, -9.35) * mm});
            skLineSegment(sketch, "E198.MirrorCS", {"start": v(-140.8, -3.35) * mm, "end": v(-140.8, -9.35) * mm});
            skLineSegment(sketch, "E199.MirrorCS", {"start": v(-140.8, -3.35) * mm, "end": v(-137.8, -3.35) * mm});
            skPoint(sketch, "E200.MirrorP", {"position": v(-139.3, -6.35) * mm});
            skLineSegment(sketch, "E201.MirrorCS", {"start": v(-140.8, -9.35) * mm, "end": v(-134.87, -9.35) * mm, "construction": true});
            skSolve(sketch);
        }
        {
            var Q0;
            Q0 = qSketchRegion(id + "F0", true);
            extrude(context, id + "F1", {"entities" : qUnion([Q0]), "depth" : .5 * mm});
        }
    });
